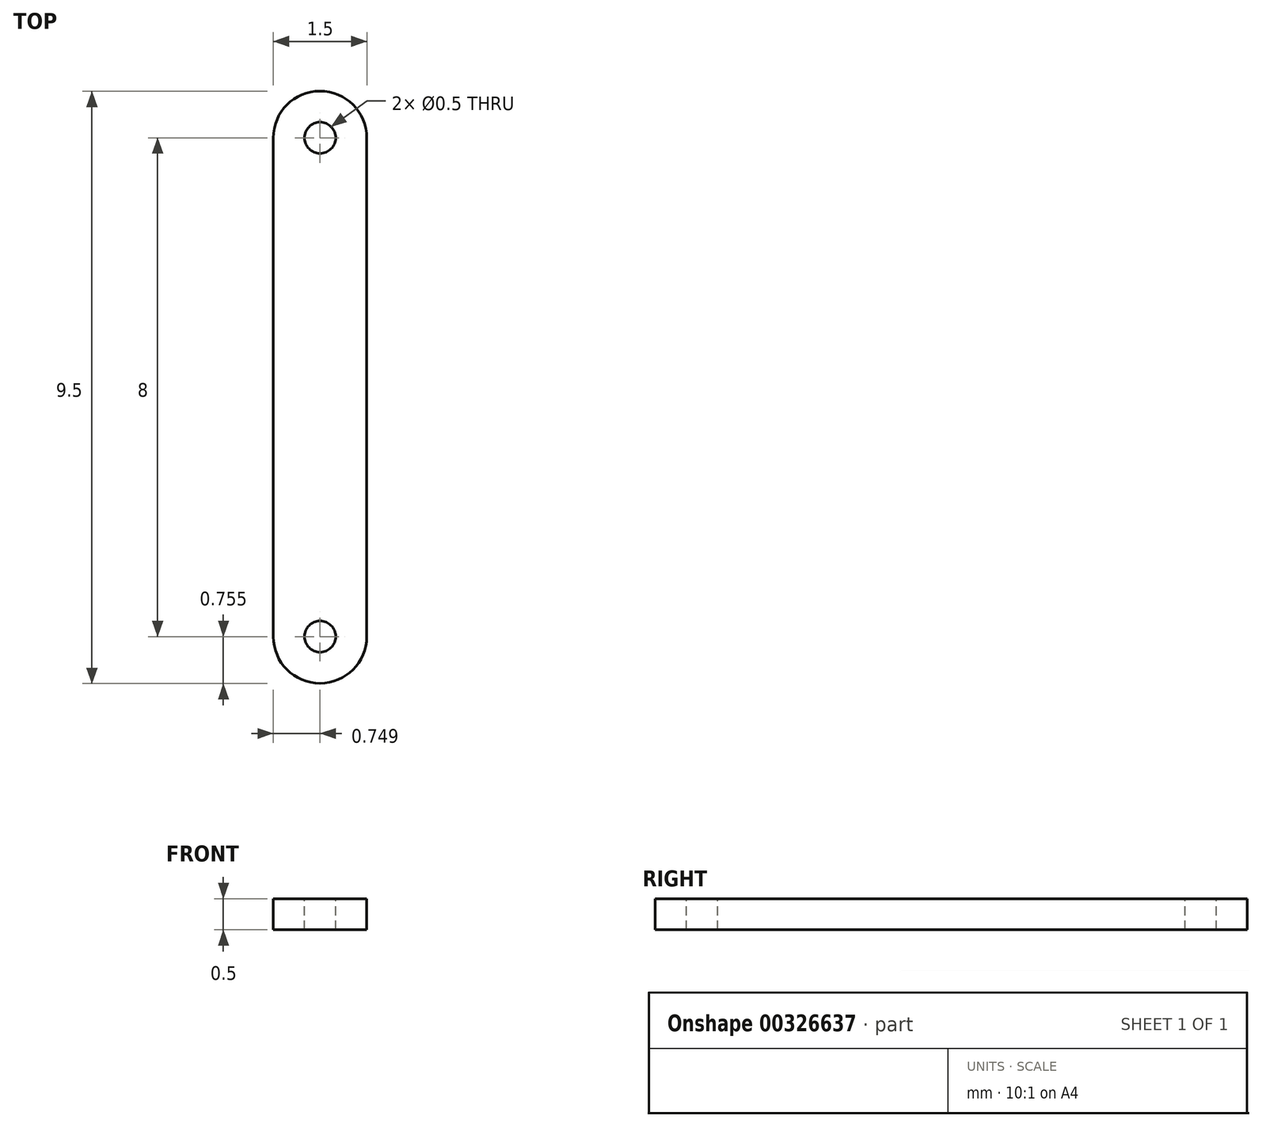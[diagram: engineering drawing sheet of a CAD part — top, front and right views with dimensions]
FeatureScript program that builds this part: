
annotation { "Feature Type Name" : "Feature", "Feature Type Description" : "" }
export const myFeature = defineFeature(function(context is Context, id is Id, definition is map)
    precondition{}
    {
        {
            var Q0;
            Q0=qCreatedBy(makeId("Top.planeOp"),FACE);
            var sketch = newSketch(context, id + "F0", { "sketchPlane" : qUnion([Q0])});
            skLineSegment(sketch, "E0", {"start": v(-29.44, 49.67) * mm, "end": v(-29.44, 41.67) * mm});
            skLineSegment(sketch, "E1", {"start": v(-27.94, 49.67) * mm, "end": v(-27.94, 41.67) * mm});
            skArc(sketch, "E2", {"start": v(-27.94, 49.67) * mm, "mid": v(-28.7, 50.42) * mm, "end": v(-29.44, 49.67) * mm});
            skArc(sketch, "E3", {"start": v(-29.44, 41.67) * mm, "mid": v(-28.7, 40.92) * mm, "end": v(-27.94, 41.67) * mm});
            skSolve(sketch);
        }
        {
            var Q0;
            Q0 = qSketchRegion(id + "F0", true);
            extrude(context, id + "F1", {"entities" : qUnion([Q0]), "depth" : 0.5 * mm});
        }
        {
            var Q0;
            Q0=makeQuery(id+"F1.opExtrude","CAP_FACE",FACE,{"disambiguationData":[OSD([sQuery(id+"F0.wireOp",EDGE,"E0"),sQuery(id+"F0.wireOp",EDGE,"E1"),sQuery(id+"F0.wireOp",EDGE,"E2"),sQuery(id+"F0.wireOp",EDGE,"E3")])],"isStart":false});
            var sketch = newSketch(context, id + "F2", { "sketchPlane" : qUnion([Q0])});
            skCircle(sketch, "E4", {"center": v(-28.7, 49.67) * mm, "radius": 0.25 * mm});
            skCircle(sketch, "E5", {"center": v(-28.7, 41.67) * mm, "radius": 0.25 * mm});
            skSolve(sketch);
        }
        {
            var Q0;
            Q0 = qSketchRegion(id + "F2", true);
            extrude(context, id + "F3", {"entities" : qUnion([Q0]), "operationType" : NewBodyOperationType.REMOVE, "oppositeDirection" : true, "depth" : 33.5 * mm});
        }
    });
